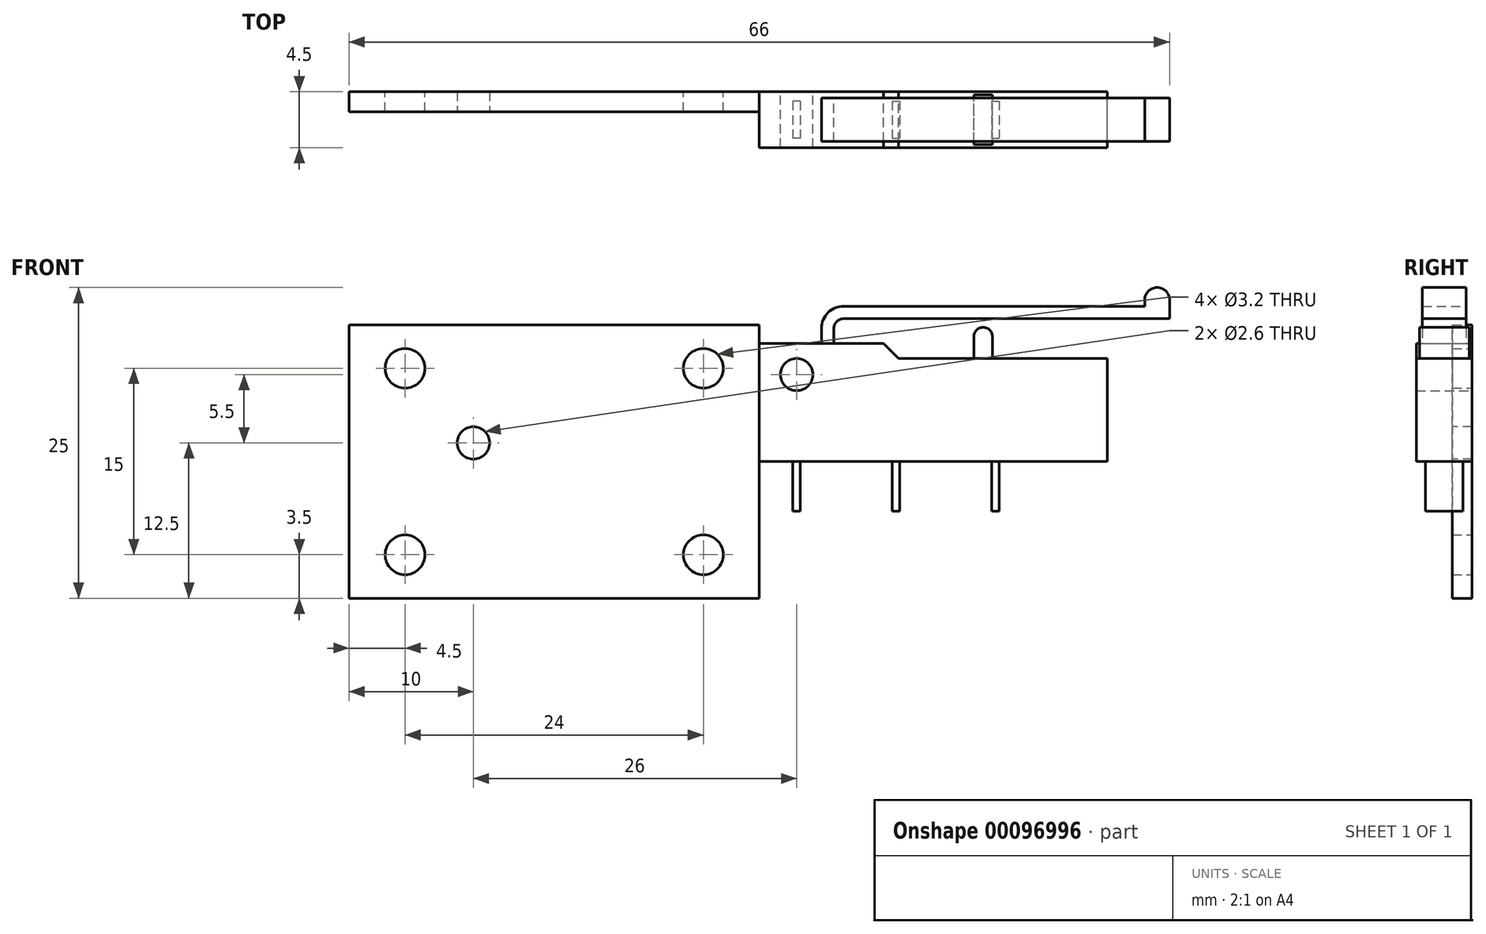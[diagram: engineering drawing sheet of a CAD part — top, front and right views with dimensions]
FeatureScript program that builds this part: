
annotation { "Feature Type Name" : "Feature", "Feature Type Description" : "" }
export const myFeature = defineFeature(function(context is Context, id is Id, definition is map)
    precondition{}
    {
        {
            var Q0;
            Q0=qCreatedBy(makeId("Front.planeOp"),FACE);
            var sketch = newSketch(context, id + "F0", { "sketchPlane" : qUnion([Q0])});
            skLineSegment(sketch, "E0.top", {"start": v(10, 9.5) * mm, "end": v(0, 9.5) * mm});
            skLineSegment(sketch, "E0.left", {"start": v(28, 0) * mm, "end": v(28, 8.3) * mm});
            skPoint(sketch, "E1.visualSharp", {"position": v(0, 9.5) * mm});
            skPoint(sketch, "E2.visualSharp", {"position": v(0, 0) * mm});
            skLineSegment(sketch, "E3", {"start": v(10, 9.5) * mm, "end": v(11.2, 8.3) * mm});
            skLineSegment(sketch, "E4", {"start": v(11.2, 8.3) * mm, "end": v(28, 8.3) * mm});
            skLineSegment(sketch, "E5", {"start": v(0, 9.5) * mm, "end": v(0, 0) * mm});
            skLineSegment(sketch, "E6", {"start": v(0, 0) * mm, "end": v(28, 0) * mm});
            skCircle(sketch, "E7", {"center": v(3, 7) * mm, "radius": 1.3 * mm});
            skSolve(sketch);
        }
        {
            var Q0;
            Q0 = qSketchRegion(id + "F0", true);
            extrude(context, id + "F1", {"entities" : qUnion([Q0]), "endBound" : BoundingType.SYMMETRIC, "depth" : 4.5 * mm});
        }
        {
            var Q0;
            Q0=qCreatedBy(makeId("Front.planeOp"),FACE);
            var sketch = newSketch(context, id + "F2", { "sketchPlane" : qUnion([Q0])});
            skLineSegment(sketch, "E8", {"start": v(0, 30.52) * mm, "end": v(0, -11.35) * mm, "construction": true});
            skLineSegment(sketch, "E9.MirrorCS", {"start": v(5, 9.5) * mm, "end": v(5, 10.7) * mm});
            skLineSegment(sketch, "E10.MirrorCS", {"start": v(6, 10.7) * mm, "end": v(6, 9.5) * mm});
            skLineSegment(sketch, "E11.MirrorCS", {"start": v(5, 9.5) * mm, "end": v(6, 9.5) * mm});
            skArc(sketch, "E12.MirrorCS", {"start": v(6, 10.7) * mm, "mid": v(6.23, 11.27) * mm, "end": v(6.8, 11.5) * mm});
            skArc(sketch, "E13.MirrorCS", {"start": v(5, 10.7) * mm, "mid": v(5.53, 11.97) * mm, "end": v(6.8, 12.5) * mm});
            skLineSegment(sketch, "E14.MirrorCS", {"start": v(33, 13) * mm, "end": v(33, 11.5) * mm});
            skLineSegment(sketch, "E15.MirrorCS", {"start": v(33, 11.5) * mm, "end": v(6.8, 11.5) * mm});
            skLineSegment(sketch, "E16.MirrorCS", {"start": v(6.8, 12.5) * mm, "end": v(31, 12.5) * mm});
            skArc(sketch, "E17", {"start": v(33, 13) * mm, "mid": v(32, 14) * mm, "end": v(31, 13) * mm});
            skLineSegment(sketch, "E18", {"start": v(31, 13) * mm, "end": v(31, 12.5) * mm});
            skSolve(sketch);
        }
        {
            var Q0;
            Q0 = qSketchRegion(id + "F2", true);
            extrude(context, id + "F3", {"entities" : qUnion([Q0]), "operationType" : NewBodyOperationType.ADD, "endBound" : BoundingType.SYMMETRIC, "depth" : 3.5 * mm});
        }
        {
            var Q0;
            Q0=qCreatedBy(makeId("Front.planeOp"),FACE);
            var sketch = newSketch(context, id + "F4", { "sketchPlane" : qUnion([Q0])});
            skArc(sketch, "E19", {"start": v(18.75, 10.05) * mm, "mid": v(18, 10.8) * mm, "end": v(17.25, 10.05) * mm});
            skLineSegment(sketch, "E20", {"start": v(18.75, 10.05) * mm, "end": v(18.75, 8.3) * mm});
            skLineSegment(sketch, "E21", {"start": v(17.25, 8.3) * mm, "end": v(17.25, 10.05) * mm});
            skLineSegment(sketch, "E22.0", {"start": v(17.25, 8.3) * mm, "end": v(18.75, 8.3) * mm});
            skPoint(sketch, "E23.orphan", {"position": v(11.2, 8.3) * mm});
            skPoint(sketch, "E24.orphan", {"position": v(28, 8.3) * mm});
            skSolve(sketch);
        }
        {
            var Q0;
            Q0 = qSketchRegion(id + "F4", true);
            extrude(context, id + "F5", {"entities" : qUnion([Q0]), "operationType" : NewBodyOperationType.ADD, "endBound" : BoundingType.SYMMETRIC, "depth" : 4 * mm});
        }
        {
            var Q0;
            Q0=qCreatedBy(makeId("Top.planeOp"),FACE);
            var sketch = newSketch(context, id + "F6", { "sketchPlane" : qUnion([Q0])});
            skLineSegment(sketch, "E25", {"start": v(19, 3.64) * mm, "end": v(19, -3.18) * mm, "construction": true});
            skLineSegment(sketch, "E26", {"start": v(11, 3.68) * mm, "end": v(11, -3.26) * mm, "construction": true});
            skLineSegment(sketch, "E27", {"start": v(3, 4.05) * mm, "end": v(3, -3.3) * mm, "construction": true});
            skLineSegment(sketch, "E28", {"start": v(-4.85, 0) * mm, "end": v(22.5, 0) * mm, "construction": true});
            skLineSegment(sketch, "E29.bottom", {"start": v(18.7, 1.5) * mm, "end": v(19.3, 1.5) * mm});
            skLineSegment(sketch, "E29.top", {"start": v(18.7, -1.5) * mm, "end": v(19.3, -1.5) * mm});
            skLineSegment(sketch, "E29.left", {"start": v(18.7, 1.5) * mm, "end": v(18.7, -1.5) * mm});
            skLineSegment(sketch, "E29.right", {"start": v(19.3, 1.5) * mm, "end": v(19.3, -1.5) * mm});
            skPoint(sketch, "E29.middle", {"position": v(19, 0) * mm});
            skLineSegment(sketch, "E30.bottom", {"start": v(10.7, 1.5) * mm, "end": v(11.3, 1.5) * mm});
            skLineSegment(sketch, "E30.top", {"start": v(10.7, -1.5) * mm, "end": v(11.3, -1.5) * mm});
            skLineSegment(sketch, "E30.left", {"start": v(10.7, 1.5) * mm, "end": v(10.7, -1.5) * mm});
            skLineSegment(sketch, "E30.right", {"start": v(11.3, 1.5) * mm, "end": v(11.3, -1.5) * mm});
            skPoint(sketch, "E30.middle", {"position": v(11, 0) * mm});
            skLineSegment(sketch, "E31.bottom", {"start": v(3.3, 1.5) * mm, "end": v(2.7, 1.5) * mm});
            skLineSegment(sketch, "E31.top", {"start": v(3.3, -1.5) * mm, "end": v(2.7, -1.5) * mm});
            skLineSegment(sketch, "E31.left", {"start": v(3.3, 1.5) * mm, "end": v(3.3, -1.5) * mm});
            skLineSegment(sketch, "E31.right", {"start": v(2.7, 1.5) * mm, "end": v(2.7, -1.5) * mm});
            skPoint(sketch, "E31.middle", {"position": v(3, 0) * mm});
            skSolve(sketch);
        }
        {
            var Q0;
            Q0 = qSketchRegion(id + "F6", true);
            extrude(context, id + "F7", {"entities" : qUnion([Q0]), "operationType" : NewBodyOperationType.ADD, "oppositeDirection" : true, "depth" : 4 * mm});
        }
        {
            var Q0;
            Q0=makeQuery(id+"F1.opExtrude","CAP_FACE",FACE,{"disambiguationData":[OSD([sQuery(id+"F0.wireOp",EDGE,"E0.top"),sQuery(id+"F0.wireOp",EDGE,"E0.left"),sQuery(id+"F0.wireOp",EDGE,"E3"),sQuery(id+"F0.wireOp",EDGE,"E4"),sQuery(id+"F0.wireOp",EDGE,"E5"),sQuery(id+"F0.wireOp",EDGE,"E6"),sQuery(id+"F0.wireOp",EDGE,"E7")])],"isStart":true});
            var sketch = newSketch(context, id + "F8", { "sketchPlane" : qUnion([Q0])});
            skLineSegment(sketch, "E32.left", {"start": v(0, -11) * mm, "end": v(0, -11) * mm});
            skCircle(sketch, "E33.MirrorC", {"center": v(28.5, -7.5) * mm, "radius": 1.6 * mm});
            skCircle(sketch, "E34.MirrorC", {"center": v(4.5, -7.5) * mm, "radius": 1.6 * mm});
            skCircle(sketch, "E35.MirrorC", {"center": v(28.5, 7.5) * mm, "radius": 1.6 * mm});
            skCircle(sketch, "E36.MirrorC", {"center": v(4.5, 7.5) * mm, "radius": 1.6 * mm});
            skLineSegment(sketch, "E37.MirrorCS", {"start": v(16.5, 11) * mm, "end": v(16.5, -11) * mm, "construction": true});
            skLineSegment(sketch, "E38.MirrorCS", {"start": v(0, 0) * mm, "end": v(35.83, 0) * mm, "construction": true});
            skLineSegment(sketch, "E39.MirrorCS", {"start": v(0, -11) * mm, "end": v(33, -11) * mm});
            skLineSegment(sketch, "E40", {"start": v(0, -11) * mm, "end": v(0, 11) * mm});
            skLineSegment(sketch, "E41", {"start": v(0, 11) * mm, "end": v(33, 11) * mm});
            skLineSegment(sketch, "E42", {"start": v(33, 11) * mm, "end": v(33, -11) * mm});
            skSolve(sketch);
        }
        {
            var Q0;
            Q0 = qSketchRegion(id + "F8", true);
            extrude(context, id + "F9", {"entities" : qUnion([Q0]), "oppositeDirection" : true, "depth" : 1.6 * mm});
        }
        {
            var Q0;
            Q0=makeQuery(id+"F9.opExtrude","CAP_FACE",FACE,{"disambiguationData":[OSD([sQuery(id+"F8.wireOp",EDGE,"E33.MirrorC"),sQuery(id+"F8.wireOp",EDGE,"E34.MirrorC"),sQuery(id+"F8.wireOp",EDGE,"E35.MirrorC"),sQuery(id+"F8.wireOp",EDGE,"E36.MirrorC"),sQuery(id+"F8.wireOp",EDGE,"E39.MirrorCS"),sQuery(id+"F8.wireOp",EDGE,"E40"),sQuery(id+"F8.wireOp",EDGE,"E41"),sQuery(id+"F8.wireOp",EDGE,"E42")])],"isStart":false});
            var sketch = newSketch(context, id + "F10", { "sketchPlane" : qUnion([Q0])});
            skCircle(sketch, "E43", {"center": v(-23, 1.5) * mm, "radius": 1.3 * mm});
            skSolve(sketch);
        }
        {
            var Q0;
            Q0 = qSketchRegion(id + "F10", true);
            extrude(context, id + "F11", {"entities" : qUnion([Q0]), "operationType" : NewBodyOperationType.REMOVE, "endBound" : BoundingType.THROUGH_ALL, "oppositeDirection" : true, "depth" : 25 * mm});
        }
    });
